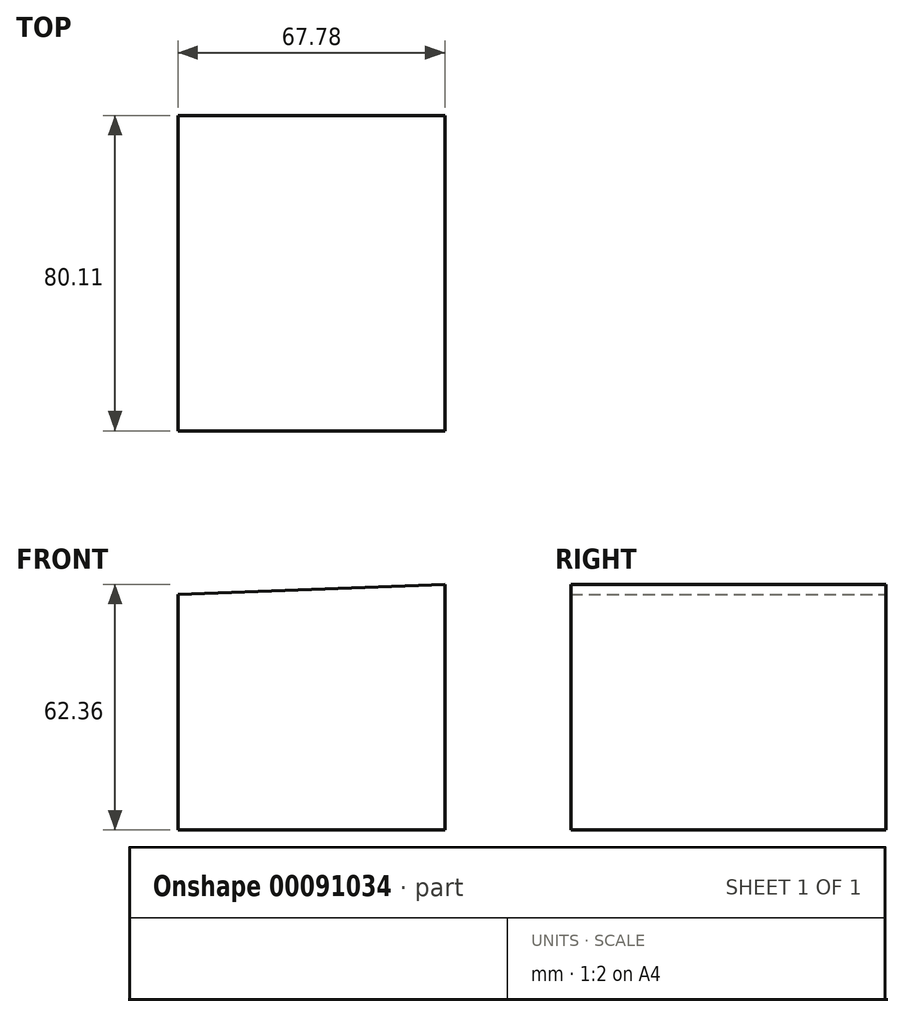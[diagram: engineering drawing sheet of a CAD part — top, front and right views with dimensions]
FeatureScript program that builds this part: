
annotation { "Feature Type Name" : "Feature", "Feature Type Description" : "" }
export const myFeature = defineFeature(function(context is Context, id is Id, definition is map)
    precondition{}
    {
        {
            var Q0;
            Q0=qCreatedBy(makeId("Front.planeOp"),FACE);
            var sketch = newSketch(context, id + "F0", { "sketchPlane" : qUnion([Q0])});
            skLineSegment(sketch, "E0", {"start": v(0, 0) * mm, "end": v(67.78, 0) * mm});
            skLineSegment(sketch, "E1", {"start": v(67.78, 0) * mm, "end": v(67.78, 62.36) * mm});
            skLineSegment(sketch, "E2", {"start": v(67.78, 62.36) * mm, "end": v(0, 59.87) * mm});
            skLineSegment(sketch, "E3", {"start": v(0, 59.87) * mm, "end": v(0, 0) * mm});
            skSolve(sketch);
        }
        {
            var Q0;
            Q0=makeQuery(id+"F0.imprint","IMPRINT",FACE,{"disambiguationData":[TD([[makeQuery(id+"F0.imprint","IMPRINT",EDGE,{"derivedFrom":sQuery(id+"F0.wireOp",EDGE,"E0")}),1.0]])]});
            extrude(context, id + "F1", {"entities" : qUnion([Q0]), "depth" : 80.11 * mm});
        }
    });
